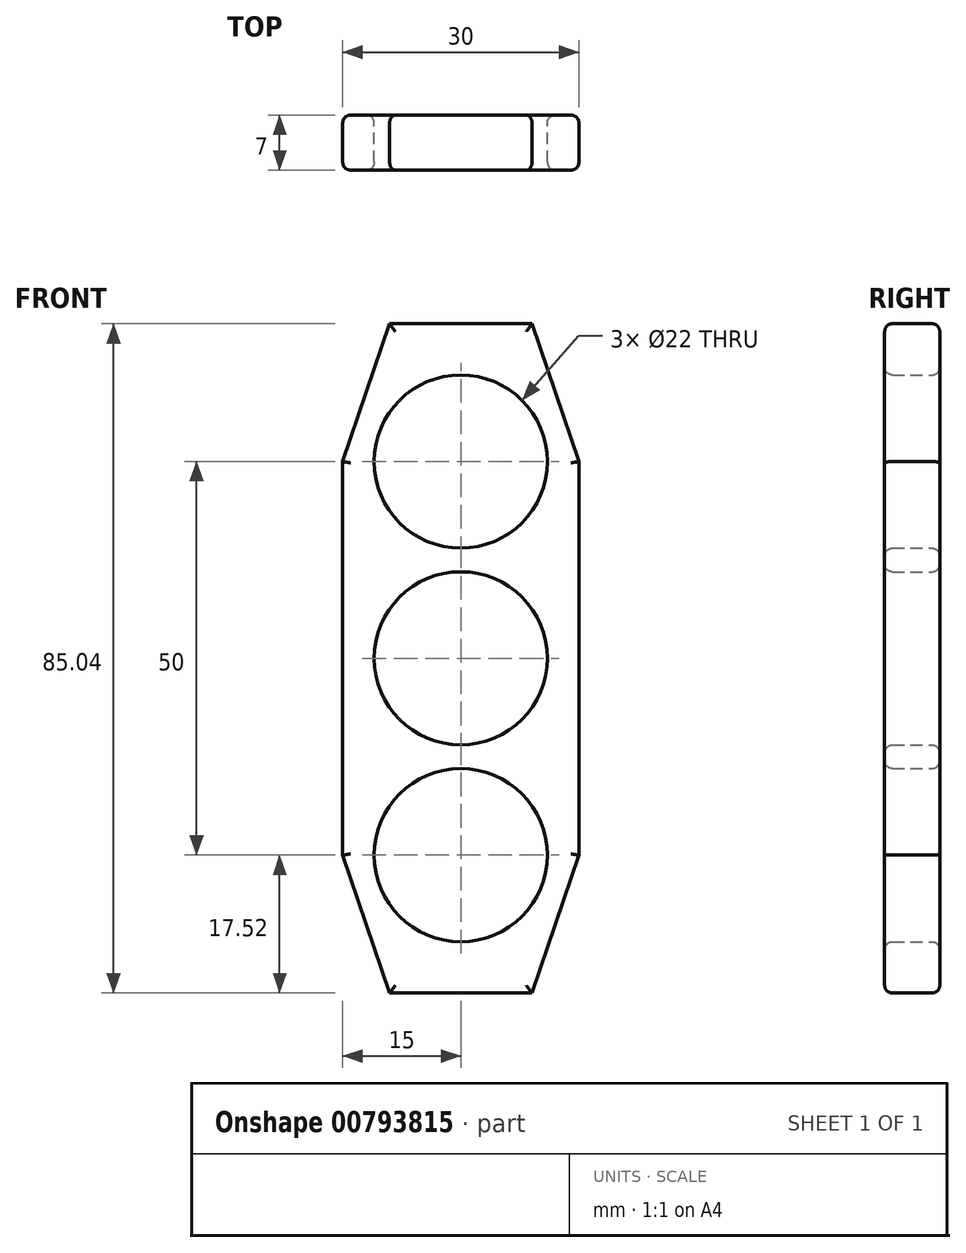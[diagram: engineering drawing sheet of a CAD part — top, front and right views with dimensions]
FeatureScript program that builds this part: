
annotation { "Feature Type Name" : "Feature", "Feature Type Description" : "" }
export const myFeature = defineFeature(function(context is Context, id is Id, definition is map)
    precondition{}
    {
        {
            var Q0;
            Q0=qCreatedBy(makeId("Front.planeOp"),FACE);
            var sketch = newSketch(context, id + "F0", { "sketchPlane" : qUnion([Q0])});
            skCircle(sketch, "E0", {"center": v(0, 0) * mm, "radius": 11 * mm});
            skLineSegment(sketch, "E1", {"start": v(0, 0) * mm, "end": v(0, 25) * mm});
            skCircle(sketch, "E2", {"center": v(0, 25) * mm, "radius": 11 * mm});
            skLineSegment(sketch, "E3", {"start": v(0, 0) * mm, "end": v(0, -25) * mm});
            skCircle(sketch, "E4", {"center": v(0, -25) * mm, "radius": 11 * mm});
            skLineSegment(sketch, "E5", {"start": v(-15, 25) * mm, "end": v(-15, -25) * mm});
            skLineSegment(sketch, "E6", {"start": v(-15, 25) * mm, "end": v(-9.04, 42.52) * mm});
            skPoint(sketch, "E7.orphan", {"position": v(15, 25) * mm});
            skLineSegment(sketch, "E8.MirrorCS", {"start": v(15, 25) * mm, "end": v(9.04, 42.52) * mm});
            skLineSegment(sketch, "E9.MirrorCS", {"start": v(15, 25) * mm, "end": v(15, -25) * mm});
            skLineSegment(sketch, "E10", {"start": v(-9.04, 42.52) * mm, "end": v(9.04, 42.52) * mm});
            skLineSegment(sketch, "E11.MirrorCS", {"start": v(-9.04, -42.52) * mm, "end": v(9.04, -42.52) * mm});
            skLineSegment(sketch, "E12.MirrorCS", {"start": v(-15, -25) * mm, "end": v(-9.04, -42.52) * mm});
            skLineSegment(sketch, "E13.MirrorCS", {"start": v(15, -25) * mm, "end": v(9.04, -42.52) * mm});
            skSolve(sketch);
        }
        {
            var Q0;
            Q0=qSketchRegion(id+"F0",true);
            extrude(context, id + "F1", {"entities" : qUnion([Q0]), "depth" : 7 * mm, "offsetDistance" : 25 * mm});
        }
        {
            var Q0;
            Q0=makeQuery(id+"F1.opExtrude","CAP_FACE",FACE,{"disambiguationData":[OSD([sQuery(id+"F0.wireOp",EDGE,"E0"),sQuery(id+"F0.wireOp",EDGE,"E2"),sQuery(id+"F0.wireOp",EDGE,"E4"),sQuery(id+"F0.wireOp",EDGE,"E5"),sQuery(id+"F0.wireOp",EDGE,"E6"),sQuery(id+"F0.wireOp",EDGE,"E8.MirrorCS"),sQuery(id+"F0.wireOp",EDGE,"E9.MirrorCS"),sQuery(id+"F0.wireOp",EDGE,"E10"),sQuery(id+"F0.wireOp",EDGE,"E11.MirrorCS"),sQuery(id+"F0.wireOp",EDGE,"E12.MirrorCS"),sQuery(id+"F0.wireOp",EDGE,"E13.MirrorCS")])],"isStart":false});
            var Q1;
            Q1=makeQuery(id+"F1.opExtrude","CAP_FACE",FACE,{"disambiguationData":[OSD([sQuery(id+"F0.wireOp",EDGE,"E0"),sQuery(id+"F0.wireOp",EDGE,"E2"),sQuery(id+"F0.wireOp",EDGE,"E4"),sQuery(id+"F0.wireOp",EDGE,"E5"),sQuery(id+"F0.wireOp",EDGE,"E6"),sQuery(id+"F0.wireOp",EDGE,"E8.MirrorCS"),sQuery(id+"F0.wireOp",EDGE,"E9.MirrorCS"),sQuery(id+"F0.wireOp",EDGE,"E10"),sQuery(id+"F0.wireOp",EDGE,"E11.MirrorCS"),sQuery(id+"F0.wireOp",EDGE,"E12.MirrorCS"),sQuery(id+"F0.wireOp",EDGE,"E13.MirrorCS")])],"isStart":true});
            fillet(context, id + "F2", {"entities" : qUnion([Q0, Q1]), "radius" : 1 * mm, "tangentPropagation" : true, "allowEdgeOverflow" : false});
        }
    });
